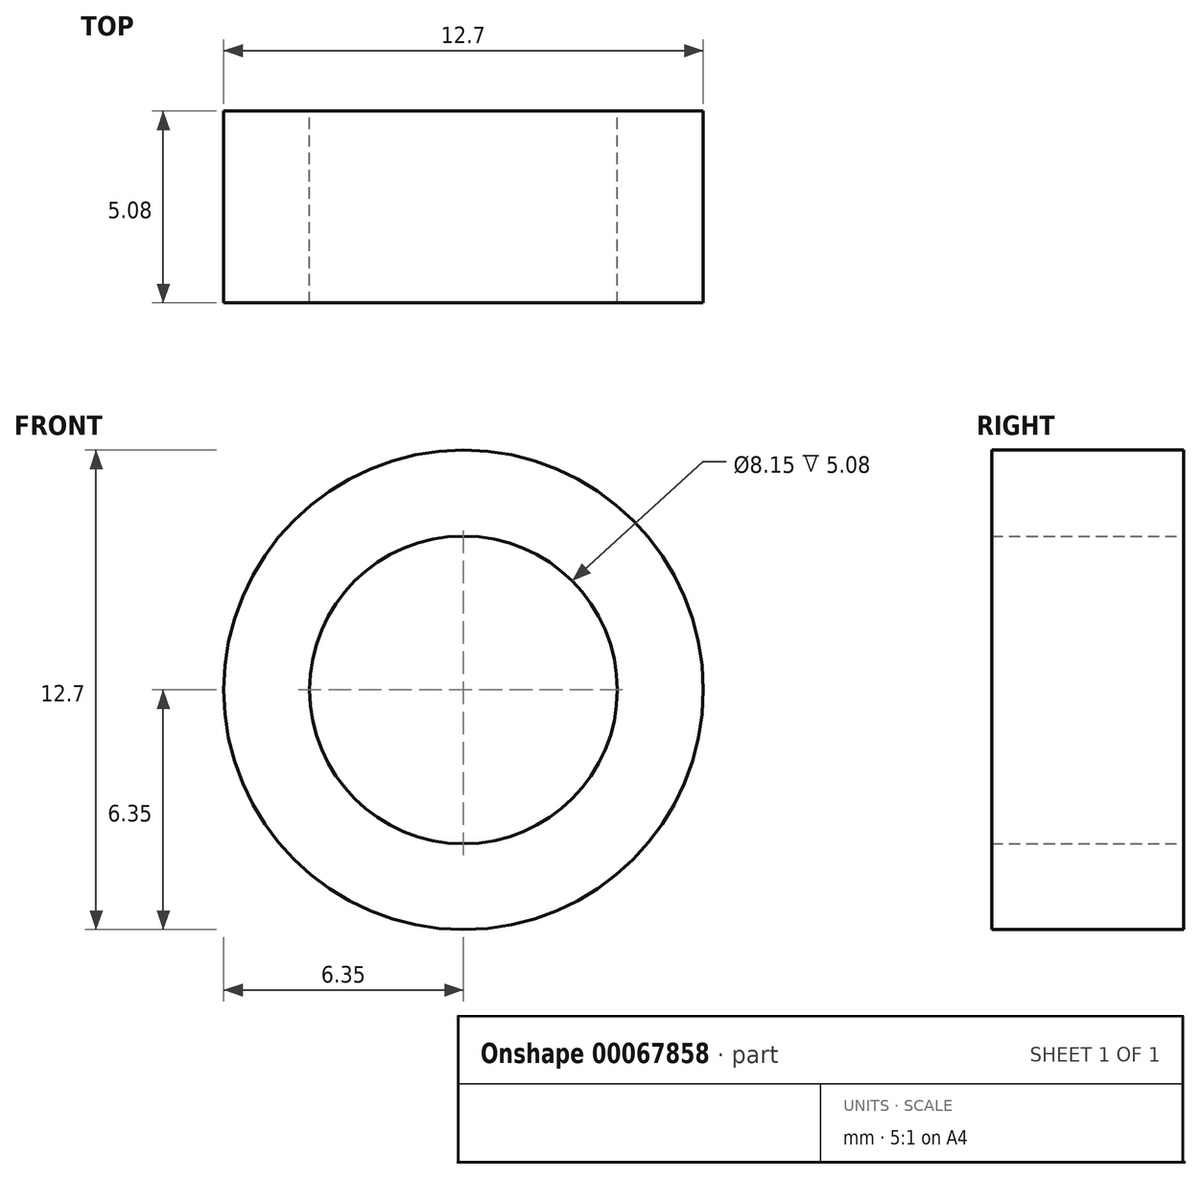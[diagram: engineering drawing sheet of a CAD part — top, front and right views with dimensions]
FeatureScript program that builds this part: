
annotation { "Feature Type Name" : "Feature", "Feature Type Description" : "" }
export const myFeature = defineFeature(function(context is Context, id is Id, definition is map)
    precondition{}
    {
        {
            var Q0;
            Q0=qCreatedBy(makeId("Front.planeOp"),FACE);
            var sketch = newSketch(context, id + "F0", { "sketchPlane" : qUnion([Q0])});
            skCircle(sketch, "E0", {"center": v(0, 0) * mm, "radius": 6.35 * mm});
            skCircle(sketch, "E1", {"center": v(0, 0) * mm, "radius": 4.07 * mm});
            skSolve(sketch);
        }
        {
            var Q0;
            Q0 = qSketchRegion(id + "F0", true);
            extrude(context, id + "F1", {"entities" : qUnion([Q0]), "depth" : 5.08 * mm});
        }
    });
